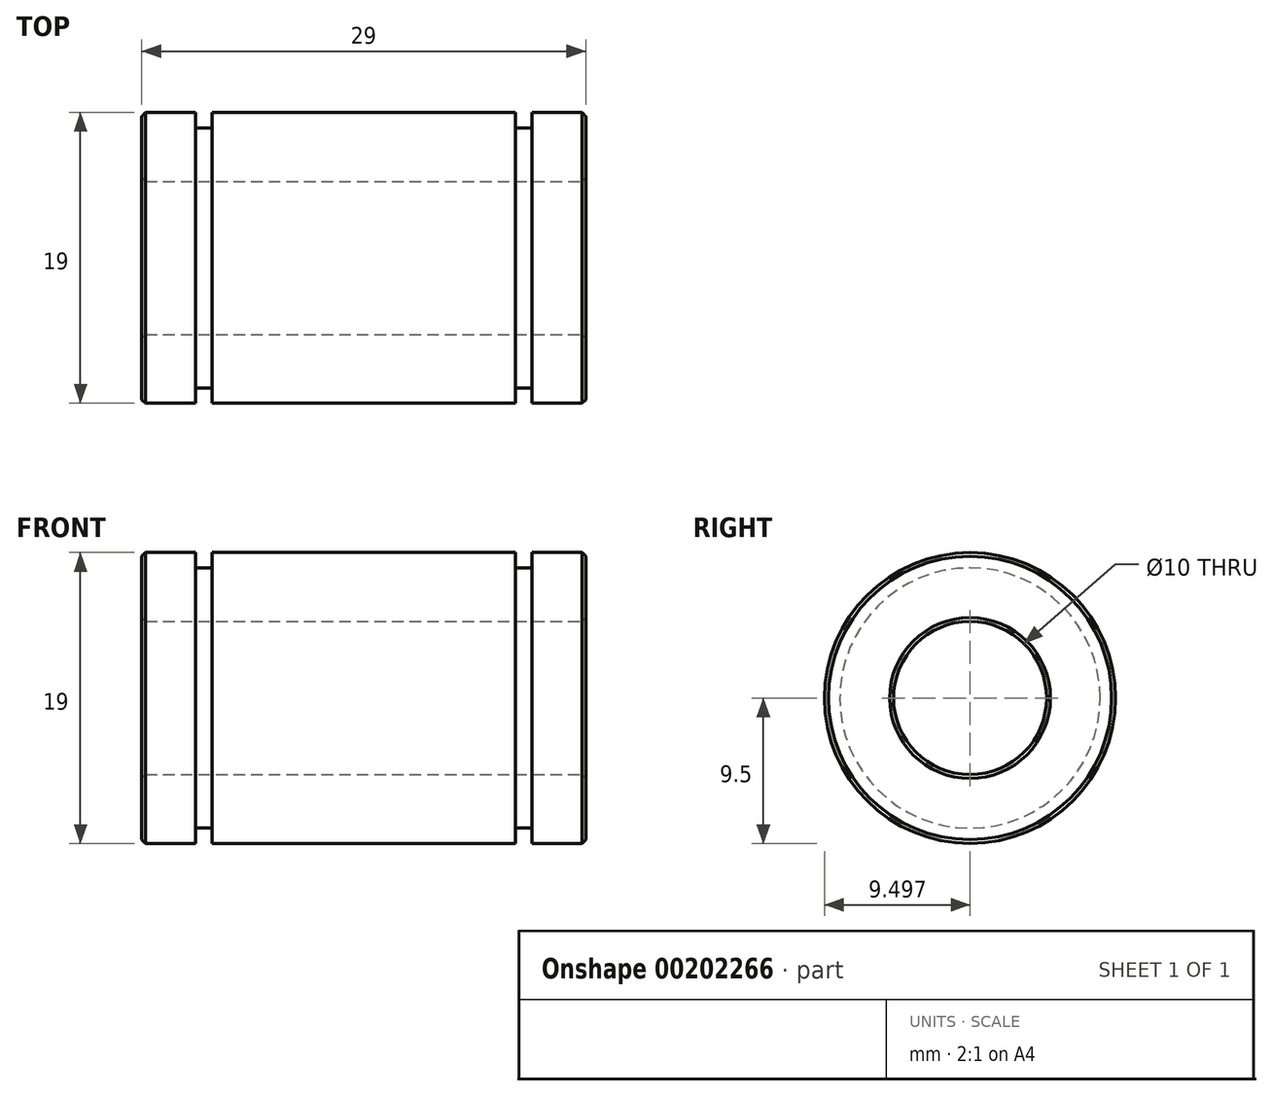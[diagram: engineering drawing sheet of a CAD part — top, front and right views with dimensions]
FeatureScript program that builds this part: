
annotation { "Feature Type Name" : "Feature", "Feature Type Description" : "" }
export const myFeature = defineFeature(function(context is Context, id is Id, definition is map)
    precondition{}
    {
        {
            var Q0;
            Q0=qCreatedBy(makeId("Top.planeOp"),FACE);
            var sketch = newSketch(context, id + "F0", { "sketchPlane" : qUnion([Q0])});
            skLineSegment(sketch, "E0", {"start": v(0, -0.83) * mm, "end": v(-29, -0.83) * mm});
            skLineSegment(sketch, "E1", {"start": v(-29, -5.83) * mm, "end": v(0, -5.83) * mm});
            skLineSegment(sketch, "E2", {"start": v(-29, -10.33) * mm, "end": v(-25.5, -10.33) * mm});
            skPoint(sketch, "E3.end.orphan", {"position": v(0, 1.34) * mm});
            skPoint(sketch, "E3.start.orphan", {"position": v(-15.77, 2.72) * mm});
            skLineSegment(sketch, "E4", {"start": v(-29, -5.83) * mm, "end": v(-29, -10.33) * mm});
            skLineSegment(sketch, "E5", {"start": v(0, -5.83) * mm, "end": v(0, -10.33) * mm});
            skLineSegment(sketch, "E6", {"start": v(-25.5, -9.33) * mm, "end": v(-25.5, -10.33) * mm});
            skLineSegment(sketch, "E7", {"start": v(-3.5, -9.33) * mm, "end": v(-3.5, -10.33) * mm});
            skLineSegment(sketch, "E8", {"start": v(-25.5, -9.33) * mm, "end": v(-24.4, -9.33) * mm});
            skLineSegment(sketch, "E9", {"start": v(-3.5, -9.33) * mm, "end": v(-4.6, -9.33) * mm});
            skLineSegment(sketch, "E10", {"start": v(-24.4, -9.33) * mm, "end": v(-24.4, -10.33) * mm});
            skLineSegment(sketch, "E11", {"start": v(-4.6, -9.33) * mm, "end": v(-4.6, -10.33) * mm});
            skLineSegment(sketch, "E12.trimOffspring", {"start": v(-24.4, -10.33) * mm, "end": v(-4.6, -10.33) * mm});
            skLineSegment(sketch, "E13.trimOffspring", {"start": v(-3.5, -10.33) * mm, "end": v(0, -10.33) * mm});
            skSolve(sketch);
        }
        {
            var Q0;
            Q0=makeQuery(id+"F0.imprint","IMPRINT",FACE,{"disambiguationData":[TD([[makeQuery(id+"F0.imprint","IMPRINT",EDGE,{"derivedFrom":sQuery(id+"F0.wireOp",EDGE,"E1")}),-1.0]])]});
            var Q1;
            Q1=sQuery(id+"F0.wireOp",EDGE,"E0");
            revolve(context, id + "F1", {"entities" : qUnion([Q0]), "axis" : qUnion([Q1]), "revolveType" : RevolveType.FULL});
        }
        {
            var Q0;
            Q0=makeQuery(id+"F1.opRevolve","SWEPT_EDGE",EDGE,{"disambiguationData":[OSD([sQuery(id+"F0.wireOp",EDGE,"E5"),sQuery(id+"F0.wireOp",EDGE,"E13.trimOffspring")])]});
            var Q1;
            Q1=makeQuery(id+"F1.opRevolve","SWEPT_EDGE",EDGE,{"disambiguationData":[OSD([sQuery(id+"F0.wireOp",EDGE,"E2"),sQuery(id+"F0.wireOp",EDGE,"E4")])]});
            var Q2;
            Q2=makeQuery(id+"F1.opRevolve","SWEPT_EDGE",EDGE,{"disambiguationData":[OSD([sQuery(id+"F0.wireOp",EDGE,"E1"),sQuery(id+"F0.wireOp",EDGE,"E4")])]});
            var Q3;
            Q3=makeQuery(id+"F1.opRevolve","SWEPT_EDGE",EDGE,{"disambiguationData":[OSD([sQuery(id+"F0.wireOp",EDGE,"E1"),sQuery(id+"F0.wireOp",EDGE,"E5")])]});
            chamfer(context, id + "F2", {"entities" : qUnion([Q0, Q1, Q2, Q3]), "width" : 0.25 * mm, "tangentPropagation" : true});
        }
    });
